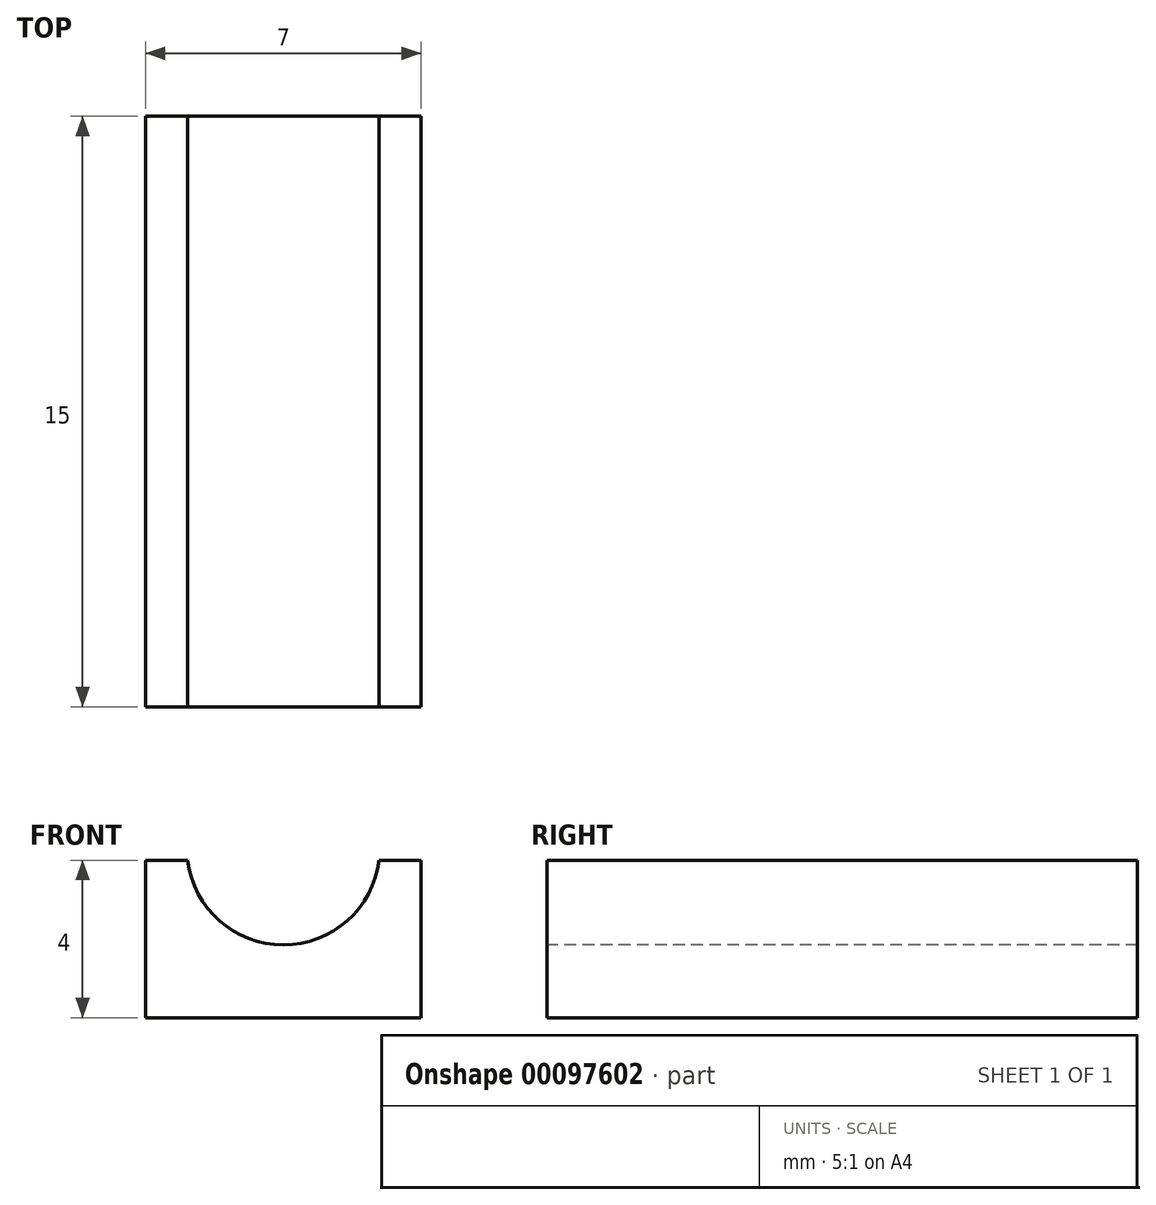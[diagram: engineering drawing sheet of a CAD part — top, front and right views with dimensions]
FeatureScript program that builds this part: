
annotation { "Feature Type Name" : "Feature", "Feature Type Description" : "" }
export const myFeature = defineFeature(function(context is Context, id is Id, definition is map)
    precondition{}
    {
        {
            var Q0;
            Q0=qCreatedBy(makeId("Top.planeOp"),FACE);
            var sketch = newSketch(context, id + "F0", { "sketchPlane" : qUnion([Q0])});
            skLineSegment(sketch, "E0.bottom", {"start": v(0, 0) * mm, "end": v(-7, 0) * mm});
            skLineSegment(sketch, "E0.top", {"start": v(0, 15) * mm, "end": v(-7, 15) * mm});
            skLineSegment(sketch, "E0.left", {"start": v(0, 0) * mm, "end": v(0, 15) * mm});
            skLineSegment(sketch, "E0.right", {"start": v(-7, 0) * mm, "end": v(-7, 15) * mm});
            skSolve(sketch);
        }
        {
            var Q0;
            Q0 = qSketchRegion(id + "F0", true);
            var Q1;
            Q1=makeQuery(id+"F0.imprint","IMPRINT",FACE,{"disambiguationData":[TD([[makeQuery(id+"F0.imprint","IMPRINT",EDGE,{"derivedFrom":sQuery(id+"F0.wireOp",EDGE,"E0.bottom")}),-1.0]])]});
            extrude(context, id + "F1", {"entities" : qUnion([Q0, Q1]), "depth" : 4 * mm});
        }
        {
            var Q0;
            Q0=makeQuery(id+"F1.opExtrude","SWEPT_FACE",FACE,{"disambiguationData":[OSD([sQuery(id+"F0.wireOp",EDGE,"E0.bottom")])]});
            var sketch = newSketch(context, id + "F2", { "sketchPlane" : qUnion([Q0])});
            skCircle(sketch, "E1", {"center": v(-3.5, 4.3) * mm, "radius": 2.45 * mm});
            skLineSegment(sketch, "E2", {"start": v(-3.5, 0) * mm, "end": v(-3.5, 8.66) * mm, "construction": true});
            skPoint(sketch, "E2.endSnap0", {"position": v(-3.5, 4) * mm});
            skSolve(sketch);
        }
        {
            var Q0;
            {var subQ0=sQuery(id+"F2.wireOp",EDGE,"E1");var subQ1=makeQuery(id+"F1.opExtrude","CAP_EDGE",EDGE,{"disambiguationData":[OSD([sQuery(id+"F0.wireOp",EDGE,"E0.bottom")])],"isStart":false});var subQ2=makeQuery(id+"F2.imprint","INTERSECT",VERTEX,{"disambiguationData":[OD(0.0)],"derivedFrom":[subQ1,subQ0]});Q0=makeQuery(id+"F2.imprint","IMPRINT",FACE,{"disambiguationData":[TD([[makeQuery(id+"F2.imprint","IMPRINT",EDGE,{"disambiguationData":[TD([[subQ2,-1.0]])],"derivedFrom":subQ0}),1.0]])]});}
            var Q1;
            {var subQ0=sQuery(id+"F2.wireOp",EDGE,"E1");var subQ1=makeQuery(id+"F1.opExtrude","CAP_EDGE",EDGE,{"disambiguationData":[OSD([sQuery(id+"F0.wireOp",EDGE,"E0.bottom")])],"isStart":false});var subQ2=makeQuery(id+"F2.imprint","INTERSECT",VERTEX,{"disambiguationData":[OD(0.0)],"derivedFrom":[subQ1,subQ0]});Q1=makeQuery(id+"F2.imprint","IMPRINT",FACE,{"disambiguationData":[TD([[makeQuery(id+"F2.imprint","IMPRINT",EDGE,{"disambiguationData":[TD([[subQ2,1.0]])],"derivedFrom":subQ0}),1.0]])]});}
            extrude(context, id + "F3", {"entities" : qUnion([Q0, Q1]), "operationType" : NewBodyOperationType.REMOVE, "endBound" : BoundingType.THROUGH_ALL, "oppositeDirection" : true, "depth" : 25 * mm});
        }
    });
